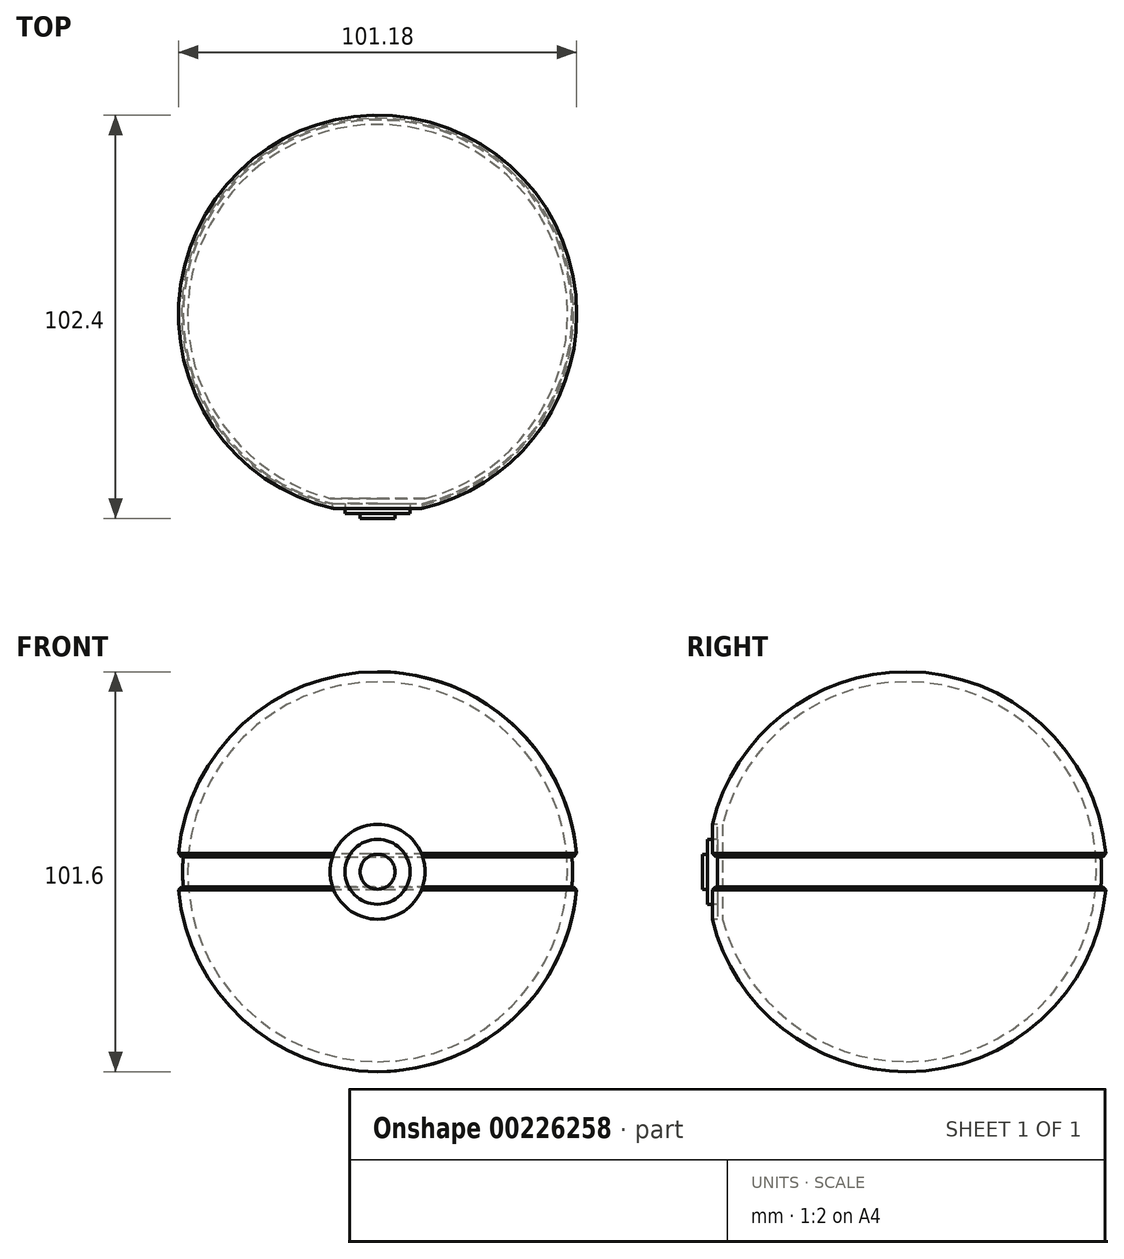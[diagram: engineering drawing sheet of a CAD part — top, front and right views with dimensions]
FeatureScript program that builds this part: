
annotation { "Feature Type Name" : "Feature", "Feature Type Description" : "" }
export const myFeature = defineFeature(function(context is Context, id is Id, definition is map)
    precondition{}
    {
        {
            var Q0;
            Q0=qCreatedBy(makeId("Front.planeOp"),FACE);
            var sketch = newSketch(context, id + "F0", { "sketchPlane" : qUnion([Q0])});
            skArc(sketch, "E0", {"start": v(50.66, 3.81) * mm, "mid": v(34.55, 37.24) * mm, "end": v(0, 50.8) * mm});
            skLineSegment(sketch, "E1", {"start": v(48.26, 0) * mm, "end": v(49.53, 0) * mm});
            skLineSegment(sketch, "E2", {"start": v(0, 48.26) * mm, "end": v(0, 50.8) * mm});
            skLineSegment(sketch, "E3", {"start": v(49.38, 3.81) * mm, "end": v(50.66, 3.81) * mm});
            skArc(sketch, "E4", {"start": v(49.53, 0) * mm, "mid": v(49.5, 1.9) * mm, "end": v(49.38, 3.81) * mm});
            skArc(sketch, "E5", {"start": v(48.26, 0) * mm, "mid": v(34.12, 34.12) * mm, "end": v(0, 48.26) * mm});
            skSolve(sketch);
        }
        {
            var Q0;
            Q0=qSketchRegion(id+"F0",true);
            var Q1;
            Q1=sQuery(id+"F0.wireOp",EDGE,"E2");
            revolve(context, id + "F1", {"entities" : qUnion([Q0]), "axis" : qUnion([Q1]), "revolveType" : RevolveType.FULL});
        }
        {
            var Q0;
            Q0=makeQuery(id+"F1.opRevolve","SWEPT_BODY",BODY,{"disambiguationData":[OSD([sQuery(id+"F0.wireOp",EDGE,"E0"),sQuery(id+"F0.wireOp",EDGE,"E1"),sQuery(id+"F0.wireOp",EDGE,"E2"),sQuery(id+"F0.wireOp",EDGE,"E3"),sQuery(id+"F0.wireOp",EDGE,"E4"),sQuery(id+"F0.wireOp",EDGE,"E5")])]});
            var Q1;
            Q1=qCreatedBy(makeId("Top.planeOp"),FACE);
            mirror(context, id + "F2", {"entities" : qUnion([Q0]), "mirrorPlane" : qUnion([Q1])});
        }
        {
            var Q0;
            Q0=qCreatedBy(makeId("Front.planeOp"),FACE);
            var sketch = newSketch(context, id + "F3", { "sketchPlane" : qUnion([Q0])});
            skCircle(sketch, "E6", {"center": v(0, 0) * mm, "radius": 12.06 * mm});
            skSolve(sketch);
        }
        {
            var Q0;
            Q0=qSketchRegion(id+"F3",true);
            extrude(context, id + "F4", {"entities" : qUnion([Q0]), "operationType" : NewBodyOperationType.REMOVE, "depth" : 60.2 * mm});
        }
        {
            var Q0;
            Q0=makeQuery(id+"F4.boolean.opBoolean","INTERSECT",EDGE,{"derivedFrom":[makeQuery(id+"F1.opRevolve","SWEPT_FACE",FACE,{"disambiguationData":[OSD([sQuery(id+"F0.wireOp",EDGE,"E5")])]}),makeQuery(id+"F4.opExtrude","SWEPT_FACE",FACE,{"disambiguationData":[OSD([sQuery(id+"F3.wireOp",EDGE,"E6")])]})]});
            cPoint(context, id + "F5", {"entities" : qUnion([Q0]), "parameter" : 0.5});
        }
        {
            var Q0;
            Q0=qCreatedBy(makeId("Front.planeOp"),FACE);
            var Q1;
            Q1=qCreatedBy(id+"F5",VERTEX);
            cPlane(context, id + "F6", {"entities" : qUnion([Q0, Q1]), "cplaneType" : CPlaneType.PLANE_POINT, "offset" : 25.4 * mm, "width" : 152.4 * mm, "height" : 152.4 * mm});
        }
        {
            var Q0;
            Q0=qCreatedBy(id+"F6.planeOp",FACE);
            var sketch = newSketch(context, id + "F7", { "sketchPlane" : qUnion([Q0])});
            skCircle(sketch, "E7", {"center": v(0, 0) * mm, "radius": 12.07 * mm});
            skSolve(sketch);
        }
        {
            var Q0;
            Q0=qSketchRegion(id+"F7",true);
            extrude(context, id + "F8", {"entities" : qUnion([Q0]), "operationType" : NewBodyOperationType.ADD, "depth" : 3.8 * mm});
        }
        {
            var Q0;
            Q0=makeQuery(id+"F8.opExtrude","CAP_FACE",FACE,{"disambiguationData":[OSD([sQuery(id+"F7.wireOp",EDGE,"E7")])],"isStart":false});
            var sketch = newSketch(context, id + "F9", { "sketchPlane" : qUnion([Q0])});
            skCircle(sketch, "E8", {"center": v(0, 0) * mm, "radius": 12.07 * mm});
            skCircle(sketch, "E9", {"center": v(0, 0) * mm, "radius": 8.26 * mm});
            skSolve(sketch);
        }
        {
            var Q0;
            Q0=qSketchRegion(id+"F9",true);
            var Q1;
            Q1=makeQuery(id+"F4.boolean.opBoolean","INTERSECT",VERTEX,{"disambiguationData":[OD(1.0)],"derivedFrom":[makeQuery(id+"F1.opRevolve","SWEPT_FACE",FACE,{"disambiguationData":[OSD([sQuery(id+"F0.wireOp",EDGE,"E3")])]}),makeQuery(id+"F1.opRevolve","SWEPT_FACE",FACE,{"disambiguationData":[OSD([sQuery(id+"F0.wireOp",EDGE,"E4")])]}),makeQuery(id+"F4.opExtrude","SWEPT_FACE",FACE,{"disambiguationData":[OSD([sQuery(id+"F3.wireOp",EDGE,"E6")])]})]});
            extrude(context, id + "F10", {"entities" : qUnion([Q0]), "operationType" : NewBodyOperationType.REMOVE, "endBound" : BoundingType.UP_TO_VERTEX, "oppositeDirection" : true, "endBoundEntityVertex" : qUnion([Q1]), "depth" : 25.4 * mm});
        }
        {
            var Q0;
            Q0=makeQuery(id+"F8.opExtrude","CAP_FACE",FACE,{"disambiguationData":[OSD([sQuery(id+"F7.wireOp",EDGE,"E7")])],"isStart":false});
            var sketch = newSketch(context, id + "F11", { "sketchPlane" : qUnion([Q0])});
            skCircle(sketch, "E10.0", {"center": v(0, 0) * mm, "radius": 4.45 * mm});
            skCircle(sketch, "E11.0", {"center": v(0, 0) * mm, "radius": 10.8 * mm});
            skSolve(sketch);
        }
        {
            var Q0;
            Q0=makeQuery(id+"F11.imprint","IMPRINT",FACE,{"disambiguationData":[TD([[makeQuery(id+"F11.imprint","IMPRINT",EDGE,{"derivedFrom":sQuery(id+"F11.wireOp",EDGE,"E10.0")}),1.0]])]});
            extrude(context, id + "F12", {"entities" : qUnion([Q0]), "operationType" : NewBodyOperationType.ADD, "depth" : 1.27 * mm});
        }
        {
            var Q0;
            Q0=makeQuery(id+"F2.opPattern","COPY",EDGE,{"derivedFrom":makeQuery(id+"F1.opRevolve","SWEPT_EDGE",EDGE,{"disambiguationData":[OSD([sQuery(id+"F0.wireOp",EDGE,"E0"),sQuery(id+"F0.wireOp",EDGE,"E3")])]}),"instanceName":"1"});
            var Q1;
            Q1=makeQuery(id+"F1.opRevolve","SWEPT_EDGE",EDGE,{"disambiguationData":[OSD([sQuery(id+"F0.wireOp",EDGE,"E0"),sQuery(id+"F0.wireOp",EDGE,"E3")])]});
            var Q2;
            Q2=makeQuery(id+"F4.boolean.opBoolean","INTERSECT",EDGE,{"derivedFrom":[makeQuery(id+"F2.opPattern","COPY",FACE,{"derivedFrom":makeQuery(id+"F1.opRevolve","SWEPT_FACE",FACE,{"disambiguationData":[OSD([sQuery(id+"F0.wireOp",EDGE,"E0")])]}),"instanceName":"1"}),makeQuery(id+"F4.opExtrude","SWEPT_FACE",FACE,{"disambiguationData":[OSD([sQuery(id+"F3.wireOp",EDGE,"E6")])]})]});
            var Q3;
            Q3=makeQuery(id+"F4.boolean.opBoolean","INTERSECT",EDGE,{"derivedFrom":[makeQuery(id+"F1.opRevolve","SWEPT_FACE",FACE,{"disambiguationData":[OSD([sQuery(id+"F0.wireOp",EDGE,"E0")])]}),makeQuery(id+"F4.opExtrude","SWEPT_FACE",FACE,{"disambiguationData":[OSD([sQuery(id+"F3.wireOp",EDGE,"E6")])]})]});
            chamfer(context, id + "F13", {"entities" : qUnion([Q0, Q1, Q2, Q3]), "width" : 0.76 * mm, "tangentPropagation" : true});
        }
    });
